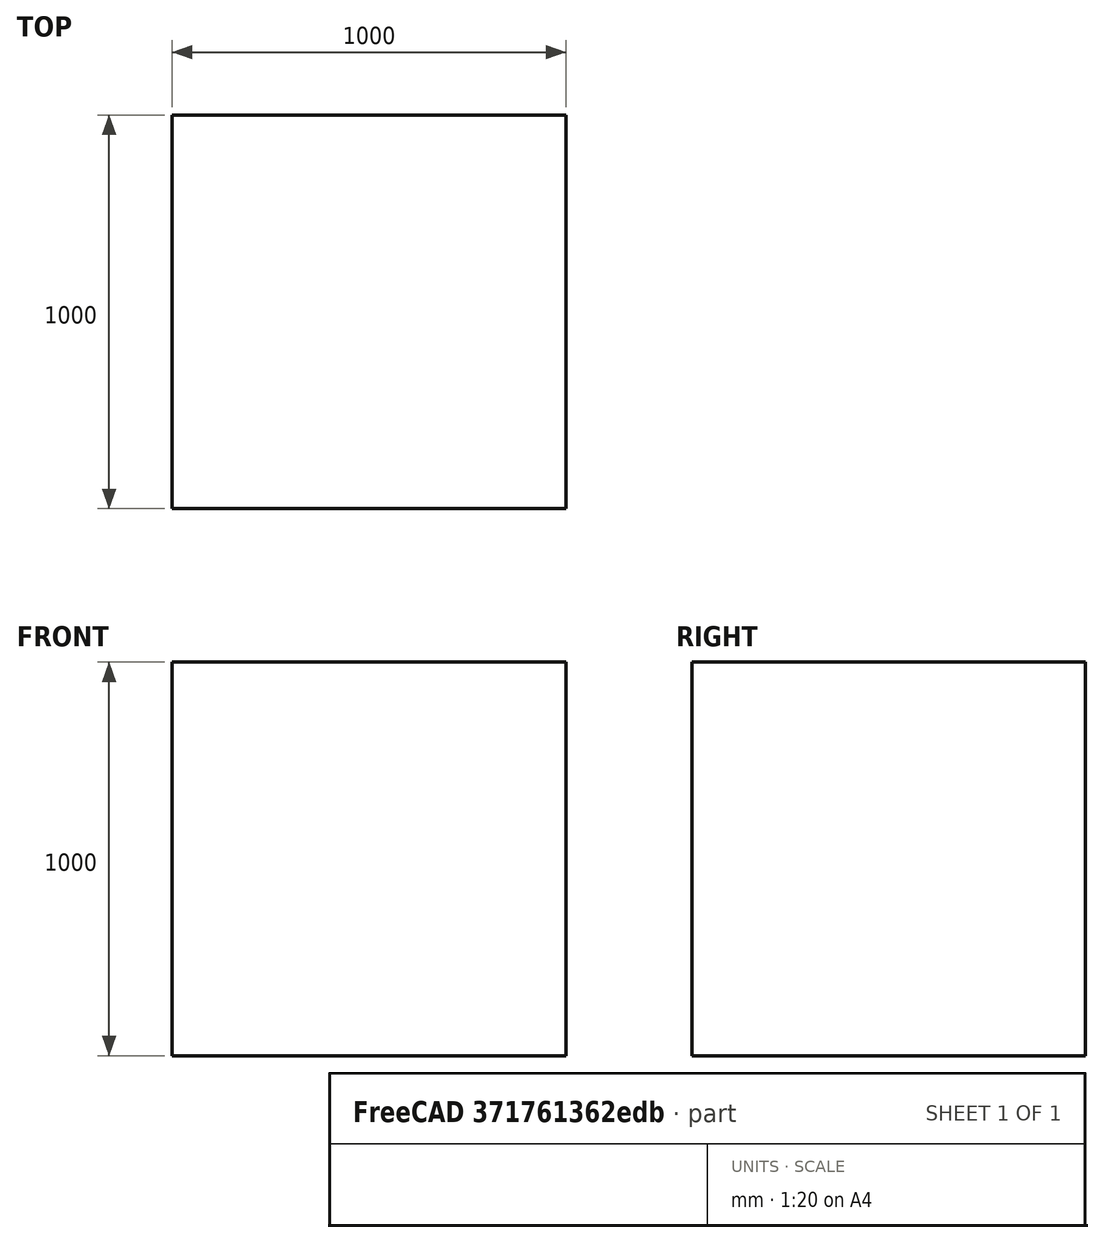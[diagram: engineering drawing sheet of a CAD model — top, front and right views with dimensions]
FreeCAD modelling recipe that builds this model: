
FCSTD DOCUMENT  (FreeCAD 0.19R)
Label: basic-box
License: All rights reserved
LicenseURL: http://en.wikipedia.org/wiki/All_rights_reserved
objects: Sketcher::SketchObject×1, PartDesign::Pad×1, PartDesign::Body×1
note: 4 computed .brp shape members not serialized (recipe doc carries the construction recipe); baked Part::Feature solids carry a one-line shape summary decoded from their .brp

FEATURE [Sketcher::SketchObject] Sketch
  FullyConstrained = true
  MapMode = 5
  Support = -> [XY_Plane]
  sketch-geometry (4):
    g0: LineSegment StartX=-500 StartY=500 StartZ=0 EndX=500 EndY=500 EndZ=0
    g1: LineSegment StartX=500 StartY=500 StartZ=0 EndX=500 EndY=-500 EndZ=0
    g2: LineSegment StartX=500 StartY=-500 StartZ=0 EndX=-500 EndY=-500 EndZ=0
    g3: LineSegment StartX=-500 StartY=-500 StartZ=0 EndX=-500 EndY=500 EndZ=0
  constraints (11):
    c: Coincident(g0,g1)
    c: Coincident(g1,g2)
    c: Coincident(g2,g3)
    c: Coincident(g3,g0)
    c: Horizontal(g0)
    c: Horizontal(g2)
    c: Vertical(g1)
    c: Vertical(g3)
    c: Symmetric(g0,g1,g-1)
    c: DistanceX(g0,g0) = 1000
    c: DistanceY(g2,g0) = 1000
FEATURE [PartDesign::Pad] Pad
  Direction = (1,1,1)
  Length = 1000
  Length2 = 100
  Profile = -> Sketch
  Type = 0
FEATURE [PartDesign::Body] Body
  Group = -> [Sketch,Pad]
  Origin = -> Origin
  Tip = -> Pad
